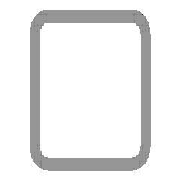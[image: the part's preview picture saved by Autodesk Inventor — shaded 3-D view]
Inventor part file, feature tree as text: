
AUTODESK INVENTOR PART (.ipt)
format: ipt  version: 2025.1 (Build 291241020, 241B)  size: 142,848 bytes
history: native  units: mm (DEFAULTED — no unit token found)
features: other x4, sketch x1, plane x1
ambient origin geometry x8: Origin, YZ Plane, XZ Plane, XY Plane, X Axis, Y Axis, Z Axis, Center Point
bodies: Solid1 (feature_tree), Body (feature_tree)
feature tree (6):
  parser-record x1  (decoder bookkeeping rows leaked as tree rows — omitted from the tree; the rows remain in map.json)
  other  "Driven Length"
  other  "Start Plane"
  other  "End Plane"
  sketch  "Sketch3"  dims[d3=1250.0mm d4=0.0mm d7=4.0mm d9=40.0mm d11=40.0mm d12=2.0mm d13=50.0mm d14=1300.0mm d15=20.0mm d16=20.0mm d17=90.0deg d18=1250.0mm]
  plane  "Work Plane3"
